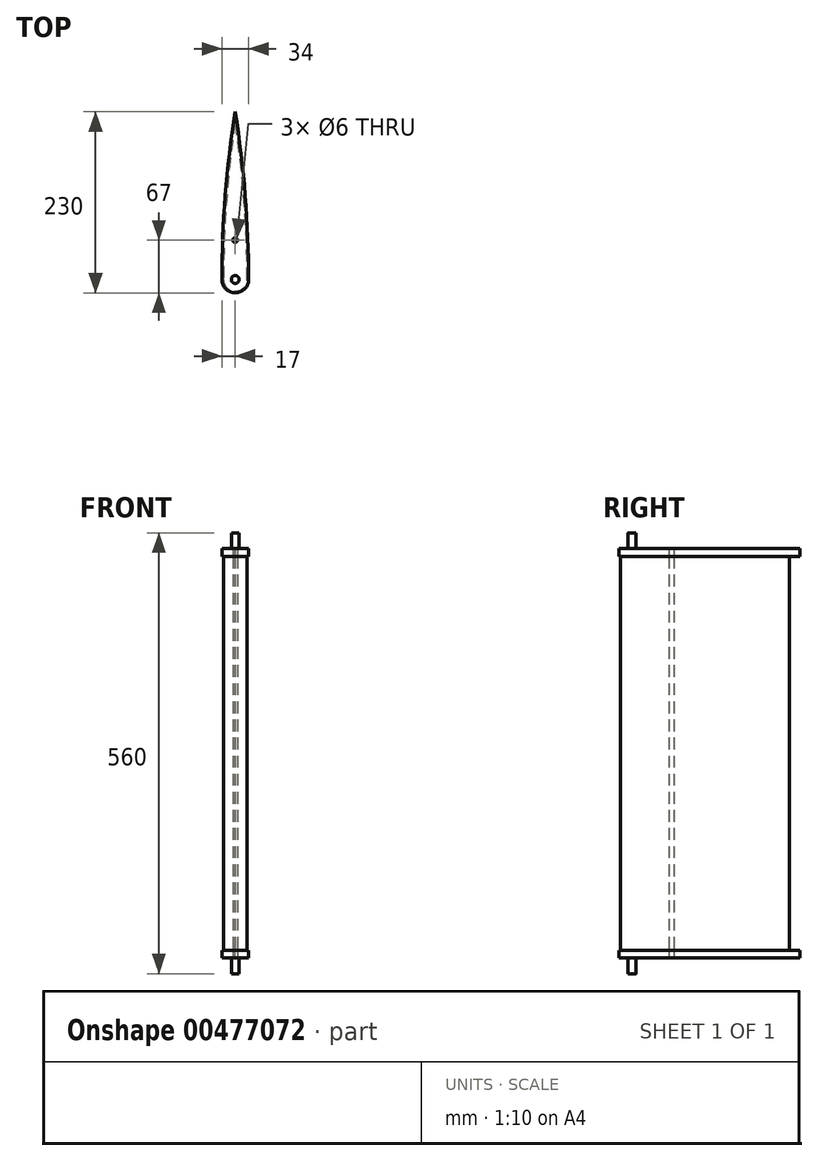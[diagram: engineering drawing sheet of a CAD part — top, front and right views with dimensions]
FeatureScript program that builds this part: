
annotation { "Feature Type Name" : "Feature", "Feature Type Description" : "" }
export const myFeature = defineFeature(function(context is Context, id is Id, definition is map)
    precondition{}
    {
        {
            var Q0;
            Q0=qCreatedBy(makeId("Top.planeOp"),FACE);
            var sketch = newSketch(context, id + "F0", { "sketchPlane" : qUnion([Q0])});
            skArc(sketch, "E0", {"start": v(-15, 0) * mm, "mid": v(0, -15) * mm, "end": v(15, 0) * mm});
            skArc(sketch, "E1", {"start": v(-15, 0) * mm, "mid": v(-11.24, 100.28) * mm, "end": v(0, 200) * mm});
            skLineSegment(sketch, "E2", {"start": v(0, 0) * mm, "end": v(0, 200) * mm, "construction": true});
            skArc(sketch, "E3.MirrorCS", {"start": v(15, 0) * mm, "mid": v(11.24, 100.28) * mm, "end": v(0, 200) * mm});
            skSolve(sketch);
        }
        {
            var Q0;
            Q0=qSketchRegion(id+"F0",true);
            extrude(context, id + "F1", {"entities" : qUnion([Q0]), "endBound" : BoundingType.SYMMETRIC, "depth" : 500 * mm});
        }
        {
            var Q0;
            Q0=makeQuery(id+"F1.opExtrude","CAP_FACE",FACE,{"disambiguationData":[OSD([sQuery(id+"F0.wireOp",EDGE,"E0"),sQuery(id+"F0.wireOp",EDGE,"E1"),sQuery(id+"F0.wireOp",EDGE,"E3.MirrorCS")])],"isStart":false});
            var sketch = newSketch(context, id + "F2", { "sketchPlane" : qUnion([Q0])});
            skArc(sketch, "E4.0", {"start": v(-17, 0) * mm, "mid": v(0, -17) * mm, "end": v(17, 0) * mm});
            skArc(sketch, "E4.1", {"start": v(0, 213) * mm, "mid": v(-12.74, 106.84) * mm, "end": v(-17, 0) * mm});
            skArc(sketch, "E4.2", {"start": v(17, 0) * mm, "mid": v(12.74, 106.84) * mm, "end": v(0, 213) * mm});
            skSolve(sketch);
        }
        {
            var Q0;
            Q0=qSketchRegion(id+"F2",true);
            extrude(context, id + "F3", {"entities" : qUnion([Q0]), "depth" : 10 * mm});
        }
        {
            var Q0;
            Q0=makeQuery(id+"F3.opExtrude","CAP_FACE",FACE,{"disambiguationData":[OSD([sQuery(id+"F2.wireOp",EDGE,"E4.0"),sQuery(id+"F2.wireOp",EDGE,"E4.1"),sQuery(id+"F2.wireOp",EDGE,"E4.2")])],"isStart":false});
            var sketch = newSketch(context, id + "F4", { "sketchPlane" : qUnion([Q0])});
            skCircle(sketch, "E5", {"center": v(0, 0) * mm, "radius": 5 * mm});
            skSolve(sketch);
        }
        {
            var Q0;
            Q0=qSketchRegion(id+"F4",true);
            extrude(context, id + "F5", {"entities" : qUnion([Q0]), "operationType" : NewBodyOperationType.ADD, "depth" : 20 * mm});
        }
        {
            var Q0;
            Q0=makeQuery(id+"F3.opExtrude","SWEPT_BODY",BODY,{"disambiguationData":[OSD([sQuery(id+"F2.wireOp",EDGE,"E4.0"),sQuery(id+"F2.wireOp",EDGE,"E4.1"),sQuery(id+"F2.wireOp",EDGE,"E4.2")])]});
            var Q1;
            Q1=qCreatedBy(makeId("Top.planeOp"),FACE);
            mirror(context, id + "F6", {"entities" : qUnion([Q0]), "mirrorPlane" : qUnion([Q1])});
        }
        {
            var Q0;
            Q0=makeQuery(id+"F6.opPattern","COPY",FACE,{"derivedFrom":makeQuery(id+"F3.opExtrude","CAP_FACE",FACE,{"disambiguationData":[OSD([sQuery(id+"F2.wireOp",EDGE,"E4.0"),sQuery(id+"F2.wireOp",EDGE,"E4.1"),sQuery(id+"F2.wireOp",EDGE,"E4.2")])],"isStart":false}),"instanceName":"1"});
            var sketch = newSketch(context, id + "F7", { "sketchPlane" : qUnion([Q0])});
            skCircle(sketch, "E6", {"center": v(0, -50) * mm, "radius": 3 * mm});
            skLineSegment(sketch, "E7", {"start": v(0, 0) * mm, "end": v(0, -50) * mm, "construction": true});
            skSolve(sketch);
        }
        {
            var Q0;
            Q0=qSketchRegion(id+"F7",true);
            extrude(context, id + "F8", {"entities" : qUnion([Q0]), "operationType" : NewBodyOperationType.REMOVE, "endBound" : BoundingType.THROUGH_ALL, "oppositeDirection" : true, "depth" : 25 * mm});
        }
    });
